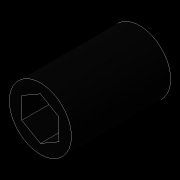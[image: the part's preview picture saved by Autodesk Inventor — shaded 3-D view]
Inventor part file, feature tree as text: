
AUTODESK INVENTOR PART (.ipt)
format: ipt  version: 2016 (Build 200138000, 138)  size: 84,480 bytes
history: native  units: in
note: dims shown in document units (in); Inventor stores cm internally (conversion verified against a paired STEP export)
features: extrude x1, sketch x1
ambient origin geometry x8: Origin, YZ Plane, XZ Plane, XY Plane, X Axis, Y Axis, Z Axis, Center Point
bodies: Solid1 (feature_tree)
feature tree (2):
  extrude  "Extrusion1"  Depth=1.0in
  sketch  "Sketch1"  dims[d0=0.375in d1=0.625in d2=1.0in d3=0.0in]
